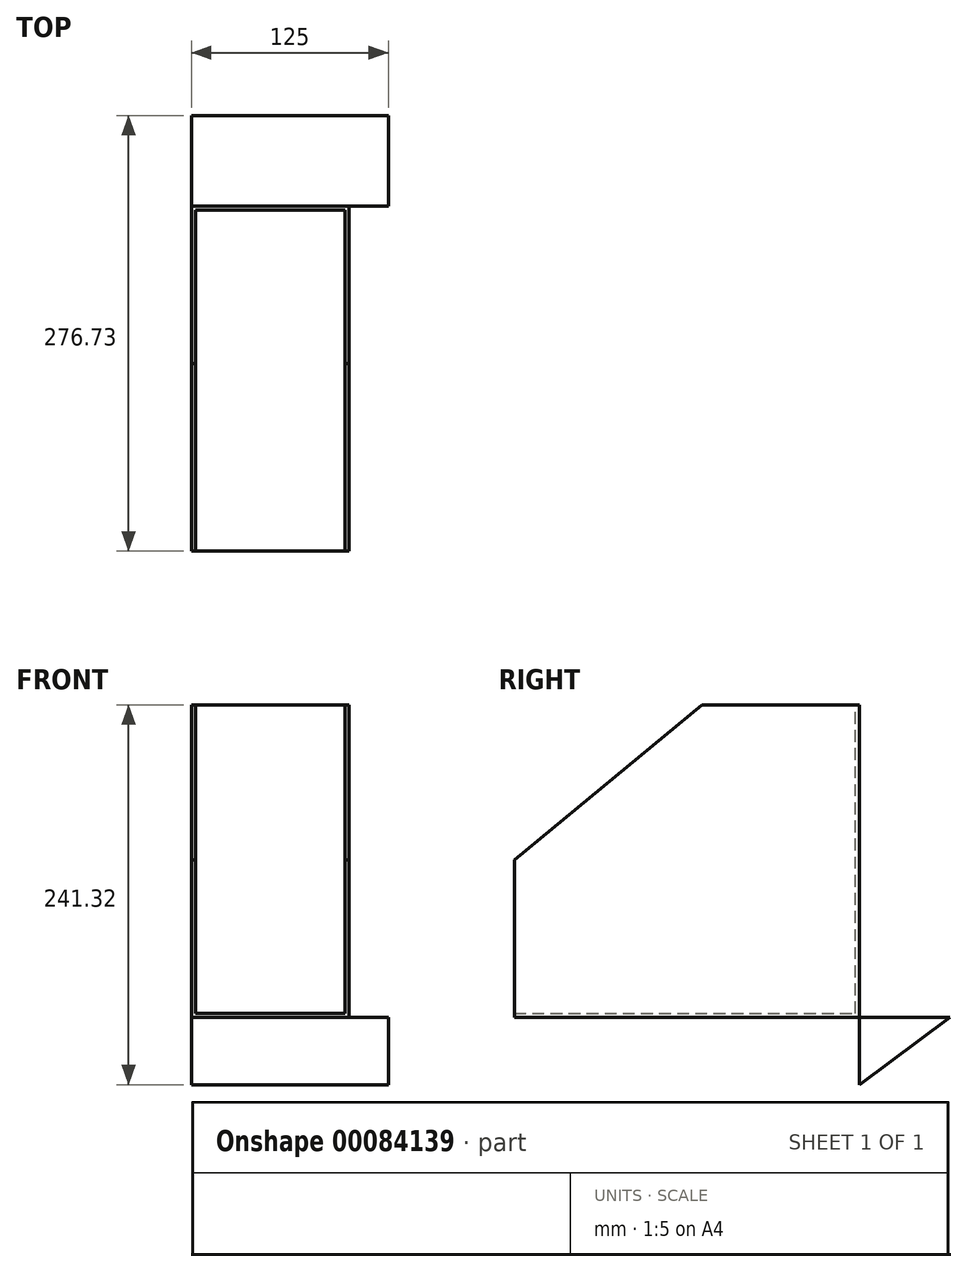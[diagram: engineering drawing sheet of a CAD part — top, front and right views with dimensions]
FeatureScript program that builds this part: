
annotation { "Feature Type Name" : "Feature", "Feature Type Description" : "" }
export const myFeature = defineFeature(function(context is Context, id is Id, definition is map)
    precondition{}
    {
        {
            var Q0;
            Q0=qCreatedBy(makeId("Right.planeOp"),FACE);
            var sketch = newSketch(context, id + "F0", { "sketchPlane" : qUnion([Q0])});
            skLineSegment(sketch, "E0", {"start": v(-122.6, -57.4) * mm, "end": v(154.13, -57.4) * mm});
            skLineSegment(sketch, "E1", {"start": v(154.84, -53.15) * mm, "end": v(154.13, -57.4) * mm});
            skLineSegment(sketch, "E2", {"start": v(96.64, -100.07) * mm, "end": v(96.64, 141.25) * mm});
            skLineSegment(sketch, "E3", {"start": v(96.64, 141.25) * mm, "end": v(-3.36, 141.25) * mm});
            skLineSegment(sketch, "E4", {"start": v(-3.36, 141.25) * mm, "end": v(-122.6, 42.6) * mm});
            skLineSegment(sketch, "E5", {"start": v(-122.6, 42.6) * mm, "end": v(-122.6, -57.4) * mm});
            skLineSegment(sketch, "E6", {"start": v(96.64, -100.07) * mm, "end": v(154.13, -57.4) * mm});
            skSolve(sketch);
        }
        {
            var Q0;
            {var subQ0=sQuery(id+"F0.wireOp",EDGE,"E3");Q0=makeQuery(id+"F0.imprint","IMPRINT",FACE,{"disambiguationData":[TD([[makeQuery(id+"F0.imprint","IMPRINT",EDGE,{"derivedFrom":subQ0}),1.0]])]});}
            extrude(context, id + "F1", {"entities" : qUnion([Q0]), "depth" : 25 * mm});
        }
        {
            var Q0;
            Q0 = qSketchRegion(id + "F0", true);
            extrude(context, id + "F2", {"entities" : qUnion([Q0]), "operationType" : NewBodyOperationType.ADD, "depth" : 100 * mm});
        }
        {
            var Q0;
            Q0=makeQuery(id+"F2.opExtrude","CAP_FACE",FACE,{"disambiguationData":[OSD([sQuery(id+"F0.wireOp",EDGE,"E0"),sQuery(id+"F0.wireOp",EDGE,"E2"),sQuery(id+"F0.wireOp",EDGE,"E6")])],"isStart":false});
            extrude(context, id + "F3", {"entities" : qUnion([Q0]), "operationType" : NewBodyOperationType.ADD, "depth" : 25 * mm});
        }
        {
            var Q0;
            {var subQ0=sQuery(id+"F0.wireOp",EDGE,"E3");Q0=makeQuery(id+"F2.boolean.opBoolean","MERGE",FACE,{"derivedFrom":[makeQuery(id+"F1.opExtrude","SWEPT_FACE",FACE,{"disambiguationData":[OSD([subQ0])]}),makeQuery(id+"F2.opExtrude","SWEPT_FACE",FACE,{"disambiguationData":[OSD([subQ0])]})]});}
            var Q1;
            {var subQ0=sQuery(id+"F0.wireOp",EDGE,"E4");Q1=makeQuery(id+"F2.boolean.opBoolean","MERGE",FACE,{"derivedFrom":[makeQuery(id+"F1.opExtrude","SWEPT_FACE",FACE,{"disambiguationData":[OSD([subQ0])]}),makeQuery(id+"F2.opExtrude","SWEPT_FACE",FACE,{"disambiguationData":[OSD([subQ0])]})]});}
            var Q2;
            {var subQ0=sQuery(id+"F0.wireOp",EDGE,"E5");Q2=makeQuery(id+"F2.boolean.opBoolean","MERGE",FACE,{"derivedFrom":[makeQuery(id+"F1.opExtrude","SWEPT_FACE",FACE,{"disambiguationData":[OSD([subQ0])]}),makeQuery(id+"F2.opExtrude","SWEPT_FACE",FACE,{"disambiguationData":[OSD([subQ0])]})]});}
            shell(context, id + "F4", {"entities" : qUnion([Q0, Q1, Q2]), "thickness" : 2.6 * mm});
        }
    });
